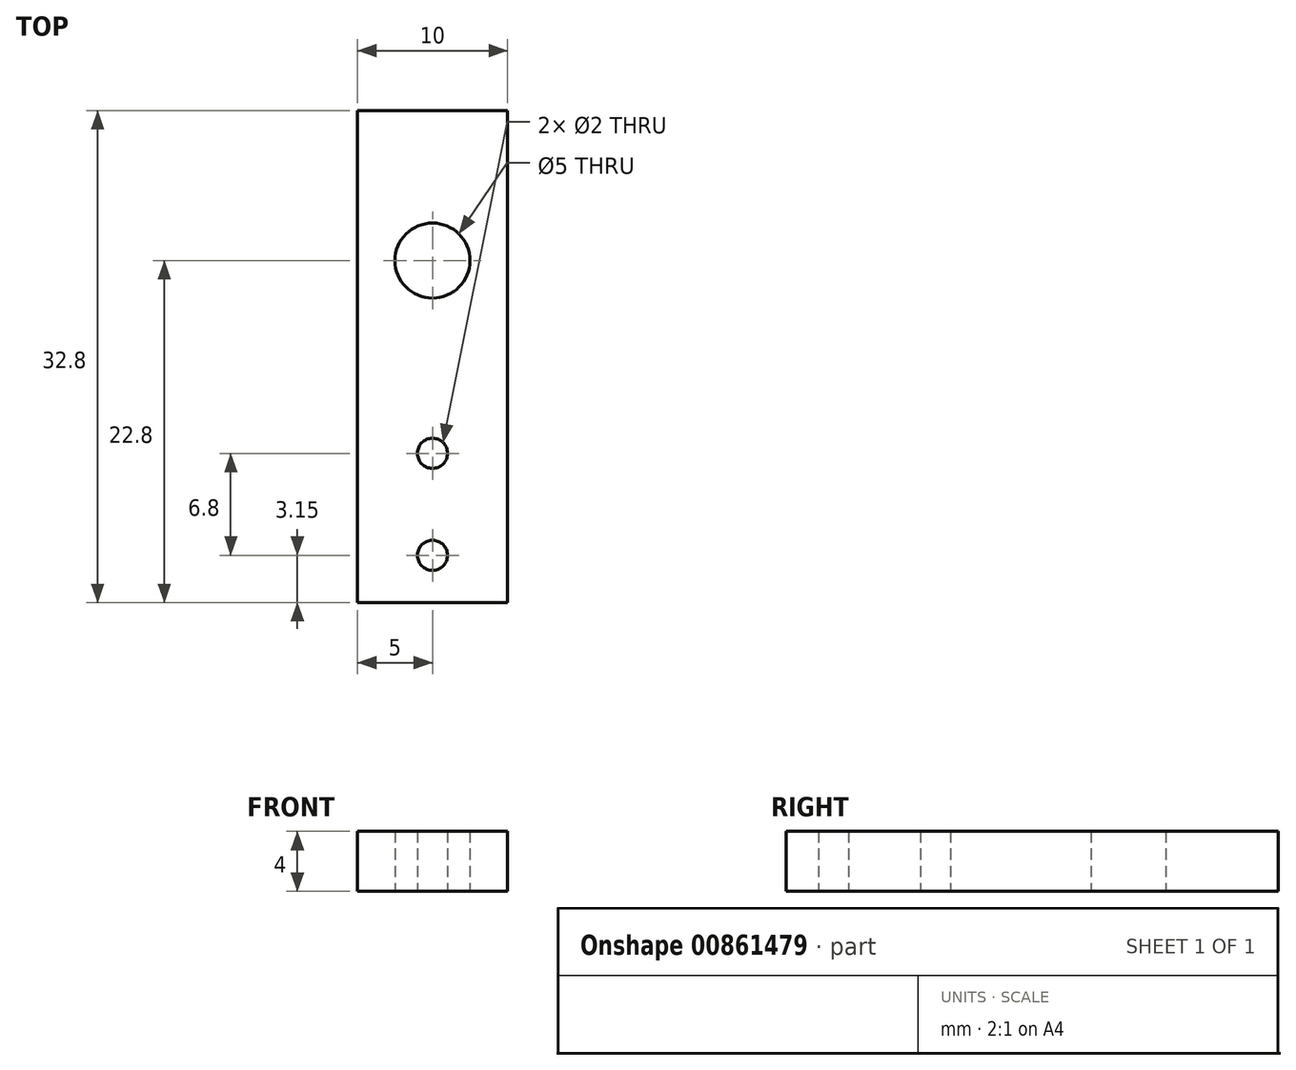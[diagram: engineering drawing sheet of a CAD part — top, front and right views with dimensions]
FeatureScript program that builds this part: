
annotation { "Feature Type Name" : "Feature", "Feature Type Description" : "" }
export const myFeature = defineFeature(function(context is Context, id is Id, definition is map)
    precondition{}
    {
        {
            var Q0;
            Q0=qCreatedBy(makeId("Top.planeOp"),FACE);
            var sketch = newSketch(context, id + "F0", { "sketchPlane" : qUnion([Q0])});
            skLineSegment(sketch, "E0.bottom", {"start": v(0, 0) * mm, "end": v(10, 0) * mm});
            skLineSegment(sketch, "E0.top", {"start": v(0, -32.8) * mm, "end": v(10, -32.8) * mm});
            skLineSegment(sketch, "E0.left", {"start": v(0, 0) * mm, "end": v(0, -32.8) * mm});
            skLineSegment(sketch, "E0.right", {"start": v(10, 0) * mm, "end": v(10, -32.8) * mm});
            skPoint(sketch, "E1", {"position": v(5, -10) * mm});
            skPoint(sketch, "E1.positionSnap0", {"position": v(5, 0) * mm});
            skCircle(sketch, "E2", {"center": v(5, -10) * mm, "radius": 2.5 * mm});
            skPoint(sketch, "E3", {"position": v(5, -29.65) * mm});
            skPoint(sketch, "E3.positionSnap0", {"position": v(5, -32.8) * mm});
            skPoint(sketch, "E4", {"position": v(5, -22.85) * mm});
            skCircle(sketch, "E5", {"center": v(5, -22.85) * mm, "radius": 1 * mm});
            skCircle(sketch, "E6", {"center": v(5, -29.65) * mm, "radius": 1 * mm});
            skSolve(sketch);
        }
        {
            var Q0;
            Q0=qSketchRegion(id+"F0",true);
            extrude(context, id + "F1", {"entities" : qUnion([Q0]), "depth" : 4 * mm, "offsetDistance" : 25 * mm});
        }
    });
